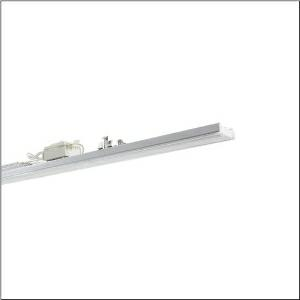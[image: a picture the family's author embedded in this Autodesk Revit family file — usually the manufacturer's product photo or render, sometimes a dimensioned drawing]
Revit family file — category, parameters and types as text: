
# Revit family: licross_21_recessed_ho_52tl12dv4l2m3c
name_source: partatom
category: Lighting Fixtures
units: mm (PartAtom-declared; Revit-internal decimal feet)

## family parameters
Cut with Voids When Loaded = No
Host = Face
Light Source = No
Part Type = Normal
Room Calculation Point = No
Round Connector Dimension = Use Diameter
Shared = No

## types (1)
- --- (1 x LED, 910 lm, 6.4 W, 4000K)
    Apparent Load = 6 VA
    CIE Flux Codes = 69 91 98 100 100
    Color Rendering = 80
    Color Temperature = 4000K
    Default Elevation = 1800 mm
    Description = Licross 21 Recessed HO, luminaire insert, of sheet steel, galvanised, coil coated, white, length: 2.250mm, width: 66mm, height: 67mm, LED rated luminous flux: 22.710lm, light colour: 840, SDCM (Standard Deviation of Colour Matching)MacAdam ≤ 3 SDCM (initial), control gear: DALI 2 (for two DALI lines), with plug, 6-pole, with phase selection, for trunking rail, 14-core, mains connection: 220..240V, AC, 50/60Hz, rated input power: 129W, for trunking rail, 14-core, internal wiring halogen-free, for emergency light function, converter,control gear: single battery element, battery: LiFePO4, 9Ah, primary optical cover: cover, of PMMA, light emission: direct distribution, primary light characteristic: symmetric, protection rating (complete): IP40, insulation class (complete): insulation class I (protective earthing), certification: CE, UKCA, protection symbol: D if used in an environment without relevant dust loads with corresponding accessories, impact resistance: IK06, permissible ambient temperature for indoor applications: +5..+30°C, standard: EN 60598-2-22, LABS conformity tested according to VDMA 24364:2018-05, reducing of maximum allowable ambient temperature of 5°C with ceiling mounting, corresponds to IFS (International Featured Standards) requirements for safety and quality in the food industry, The light source and the operating device comply with the requirements of the Ecodesign Regulation (EU) 2019/2020 and are replaceable in accordance with this regulation, packaging unit: 1 piece
    Height = 58 mm
    Lamp = 1 x LED
    Lamp Light Flux = 910 lm
    Lamp Power = 6.4 W
    Lamp count = 1
    Length = 2250 mm
    Luminous efficacy = 142 lm/W
    Manufacturer = Siteco
    ModVariant = No
    Model = 52TL12DV4L2M3C
    Mounting Place = Ceiling
    Mounting Type = Pendant
    Number of Poles = 1
    OnlyDefault = Yes
    Power Factor = 1
    Product Name = Licross 21 Recessed HO
    Product group = luminaire insert | ceiling pendant
    ProductGroupID = 901
    Protection Class = Protection class I
    Protection Degree = IP 40
    RLX_Detail_Level = 1
    RLX_Emergency_Light_Flux = 0 lm
    RLX_Emergency_Type = 0
    RLX_Emergency_Type_DB = No
    RlxData = <blob elided: 30293 chars, md5=e7804517>
    Socket = socket
    Standby Power = 0 W
    System Light Flux = 910 lm
    System Power = 6 W
    Type Comments = : emergency light operation: 3 h
    Type Image = l_1296930.jpg
    URL = http://relux.com
    VarID = @adj_109235
    Voltage = 0 V
    Weight = 0.00 kg
    Width = 66 mm

## geometry (parser evidence)
native form markers: Blend x4, Sweep x10
no freeform markers — native parametric forms only
